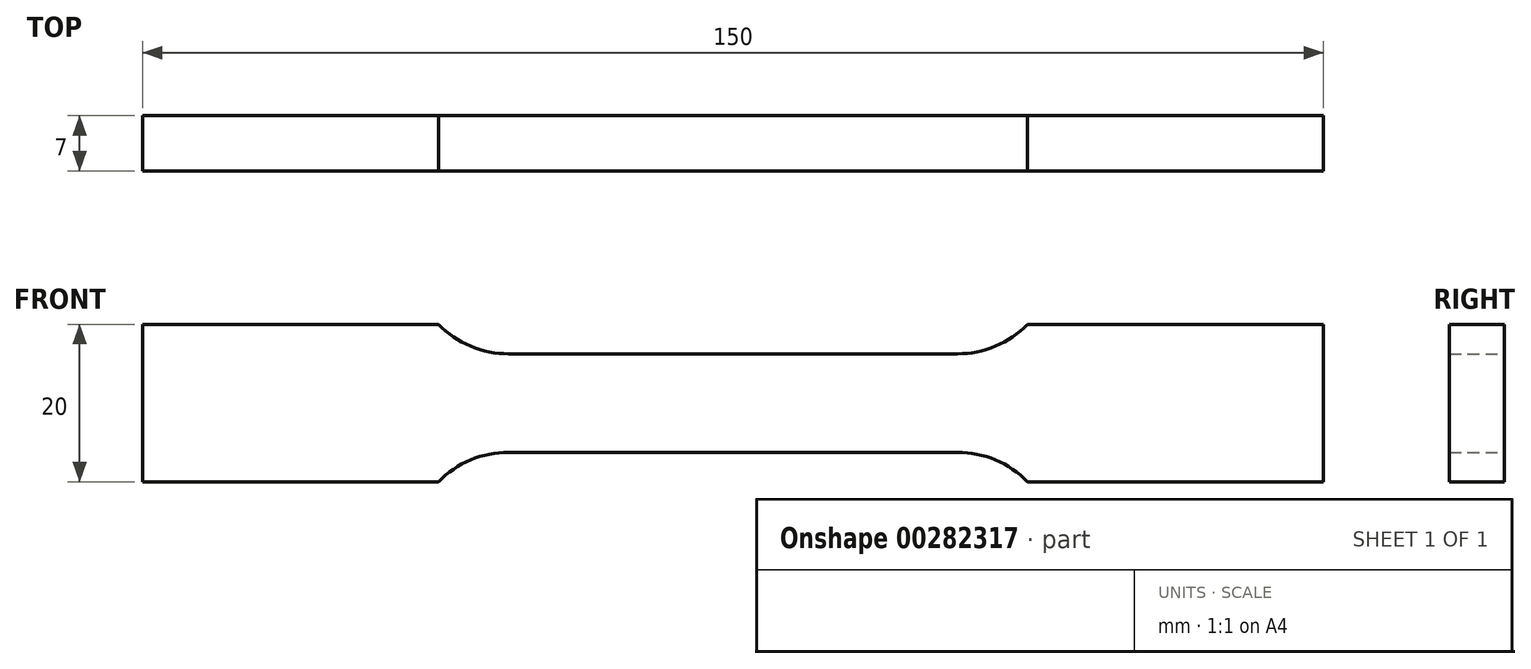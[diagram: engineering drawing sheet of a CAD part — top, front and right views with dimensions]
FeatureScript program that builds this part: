
annotation { "Feature Type Name" : "Feature", "Feature Type Description" : "" }
export const myFeature = defineFeature(function(context is Context, id is Id, definition is map)
    precondition{}
    {
        {
            var Q0;
            Q0=qCreatedBy(makeId("Front.planeOp"),FACE);
            var sketch = newSketch(context, id + "F0", { "sketchPlane" : qUnion([Q0])});
            skLineSegment(sketch, "E0", {"start": v(0, 6.25) * mm, "end": v(28.5, 6.25) * mm});
            skArc(sketch, "E1", {"start": v(28.5, 6.25) * mm, "mid": v(33.34, 7.23) * mm, "end": v(37.43, 10) * mm});
            skLineSegment(sketch, "E2", {"start": v(37.43, 10) * mm, "end": v(75, 10) * mm});
            skLineSegment(sketch, "E3.MirrorCS", {"start": v(37.43, -10) * mm, "end": v(75, -10) * mm});
            skLineSegment(sketch, "E4.MirrorCS", {"start": v(0, -6.25) * mm, "end": v(28.5, -6.25) * mm});
            skArc(sketch, "E5.MirrorCS", {"start": v(28.5, -6.25) * mm, "mid": v(33.34, -7.23) * mm, "end": v(37.43, -10) * mm});
            skLineSegment(sketch, "E6", {"start": v(75, -10) * mm, "end": v(75, 10) * mm});
            skLineSegment(sketch, "E7.MirrorCS", {"start": v(-75, -10) * mm, "end": v(-75, 10) * mm});
            skArc(sketch, "E8.MirrorCS", {"start": v(-28.5, -6.25) * mm, "mid": v(-33.34, -7.23) * mm, "end": v(-37.43, -10) * mm});
            skLineSegment(sketch, "E9.MirrorCS", {"start": v(0, -6.25) * mm, "end": v(-28.5, -6.25) * mm});
            skArc(sketch, "E10.MirrorCS", {"start": v(-28.5, 6.25) * mm, "mid": v(-33.34, 7.23) * mm, "end": v(-37.43, 10) * mm});
            skLineSegment(sketch, "E11.MirrorCS", {"start": v(0, 6.25) * mm, "end": v(-28.5, 6.25) * mm});
            skLineSegment(sketch, "E12.MirrorCS", {"start": v(-37.43, 10) * mm, "end": v(-75, 10) * mm});
            skLineSegment(sketch, "E13.MirrorCS", {"start": v(-37.43, -10) * mm, "end": v(-75, -10) * mm});
            skSolve(sketch);
        }
        {
            var Q0;
            Q0=makeQuery(id+"F0.imprint","IMPRINT",FACE,{"disambiguationData":[TD([[makeQuery(id+"F0.imprint","IMPRINT",EDGE,{"derivedFrom":sQuery(id+"F0.wireOp",EDGE,"E0")}),-1.0]])]});
            extrude(context, id + "F1", {"entities" : qUnion([Q0]), "endBound" : BoundingType.SYMMETRIC, "depth" : 7 * mm});
        }
    });
